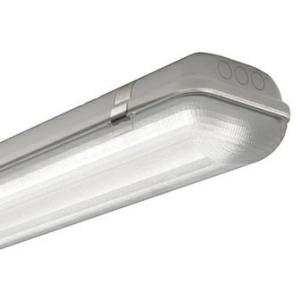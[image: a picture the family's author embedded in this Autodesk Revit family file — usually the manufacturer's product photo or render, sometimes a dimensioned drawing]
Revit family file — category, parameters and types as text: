
# Revit family: 3f_filippi_-_3f_linda_3f_filippi_-_58603_-_3f_linda_led_2x18w_ep_l1270
name_source: partatom
category: Lighting Fixtures
units: mm (PartAtom-declared; Revit-internal decimal feet)

## family parameters
Cut with Voids When Loaded = No
Host = Face
Light Source = No
Part Type = Normal
Room Calculation Point = No
Round Connector Dimension = Use Diameter
Shared = No

## types (1)
- 3F Filippi - 3F Linda (1 x LED, 6048 lm, 41 W, 4000 K)
    Apparent Load = 41 VA
    Approval mark = ENEC
    CIE Flux Codes = 46 76 93 97 100
    Color Rendering = 80
    Color Temperature = 4000 K
    Control Gear = Electronic ballast
    Default Elevation = 1800 mm
    Description = ILLUMINOTECHNICAL
Luminous efficiency 100% (DLOR 97%, ULOR 3%).
Initial luminous flux of the luminaire 6048 lm.
Emergency luminaire luminous flux BLF 9.5%.
Controlled symmetric distribution.
Installation Interdistance Transv.D = 1.52 x hu - Long.D = 1.17 x hu.
Tabular UGR (CIE 117 - 4H-8H; S=0.25H; 70/50/20): RUG 23.4 - 22.6.
Beam angle: 94° - 78°.
Luminous efficacy 148 lm/W.
Lifetime (L93/B10): 30000 h. (tq+25°C)
Lifetime (L90/B10): 50000 h. (tq+25°C)
Lifetime (L85/B10): 80000 h. (tq+25°C)
Lifetime (L80/B10): 100000 h. (tq+25°C)
Sudden decreased luminous flux after 50000 hours: 0% (C0).
Photobiological safety in compliance with IEC/TR 62778: RG0 risk exempt, (IEC 62471).
In compliance with IEC/EN 62722-2-1 - IEC/EN 62717 standards.

SOURCE
2 linear LED modules 18W/840.
Energy efficiency class (UE 2019/2020 - UE 2019/2015): D.
CIE 13.3 Colour rendering index: CRI >80 (R9 <50%).
IES TM-30 Fidelity Index: Rf = 84 Rg = 95.
CCT nominal colour temperature 4000 K.
Colour initial tolerance (MacAdam): SDCM 3.

MECHANICAL
Self-extinguishing V2 polycarbonate housing, injection moulded, RAL 7035 grey.
Ecologic anti-aging injected sealing gasket.
Diffuser in self-extinguishing V2 polycarbonate, photo-engraved interior, UV stabilised, injection moulded with smooth outer surface, tamper-proof opening.
Gear-holder reflector in hot-dip galvanised steel, painted with white polyester base.
Snug fit safety snap-lock clips for diffuser mounting in stainless steel, screwdriver opening.
Fixing brackets in stainless steel.
Possibility for technicians to access the interior of the luminaire.
Luminaire with limited surface temperature. - D - (EN 60598-2-24)
Dimensions: 1270x160 mm, height 100 mm. Weight 3.225 kg.
IP66 protection degree.
Mechanical strength to impacts IK10 (20 joule).
Glow-wire test resistance 850°C.

ELECTRICAL
Halogen Free electronic wiring 230V-50/60Hz, power factor 0.90, THD <25%, constant output current, SELV, class I, 1 driver.
Power of the luminaire 41 W.
CE - IEC 60598-1 - EN 60598-1.
EP maintained emergency wiring on board, 1h duration, 24h recharge; compliant with EN 60598-2-22, excluding high risk areas.
SAFE FLICKER: PstLM=<1 and SVM=<0.4 (IEC TR 61547-1 and IEC TR 63158), to ensure a more comfortable and safe light.
Ambient temperature from +5°C to +25°C.
Temperature class T6 max 85°C.
Relative humidity UR: <85%.

INSTALLATION
Ceiling / Suspended / Wall.
All accessories dedicated to this product are available on the Catalog and on our website www.3F-Filippi.com.

APPLICATIONS
Suitable product for food production plants (HACCP), IFS (Food Version 6), BRC (GSFS Food Version 7).
Dry, dusty indoor environments, subject to occasional water splashes.
Virtually shatterproof polycarbonate compatibly with the fumes / atmospheres that compromise the elasticity of plastic materials.
Not suitable for installation on surfaces subject to important vibrations, exposed to weather conditions, on ropes or poles.
Suitable for illumination of public car parks and parking grounds referred to DIN 67528:2018-04.

WARNING
Fixture not suitable for cold stores with an ambient temperature <5°C and/or relative humidity >85%.
Luminaire designed for disposal/recycling at end-of-life.
Replaceable (LED only) light source by a professional. Replaceable control gear by a professional.
    Height = 100 mm  [stored 0.328084 ft]
    Lamp = 1 x LED
    Lamp Light Flux = 6048 lm
    Lamp Power = 41 W
    Lamp count = 1
    Length = 1270 mm
    Lifetime = 50000 h
    Luminous efficacy = 148 lm/W
    Manufacturer = 3F Filippi
    ModVariant = No
    Model = 3F Filippi - 58603 - 3F Linda LED 2x18W EP L1270
    Mounting Place = Ceiling
    Mounting Type = Pendant
    Number of Poles = 1
    OnlyDefault = Yes
    Power Factor = 1
    Product Name = 3F Filippi - 3F Linda
    Product group = pendant luminaire
    ProductGroupID = 9
    Protection Class = Protection class I
    Protection Degree = IP 66
    RLX_Detail_Level = 1
    RLX_Emergency_Light_Flux = 0 lm
    RLX_Emergency_Type = 0
    RLX_Emergency_Type_DB = No
    RlxData = <blob elided: 71249 chars, md5=50186441>
    Socket = socket
    Standby Power = 0 W
    System Light Flux = 6048 lm
    System Power = 41 W
    Type Comments = Product without accessories
    Type Image = 3ffilippi_3f_linda_led_2x.jpg
    URL = http://relux.com
    VarID = ---
    Voltage = 0 V
    Weight = 0.00 kg
    Width = 160 mm

note: [stored X ft] marks values corroborated as IEEE doubles in the binary element streams (Revit-internal decimal feet)

## geometry (parser evidence)
native form markers: Blend x4, Sweep x9
no freeform markers — native parametric forms only
